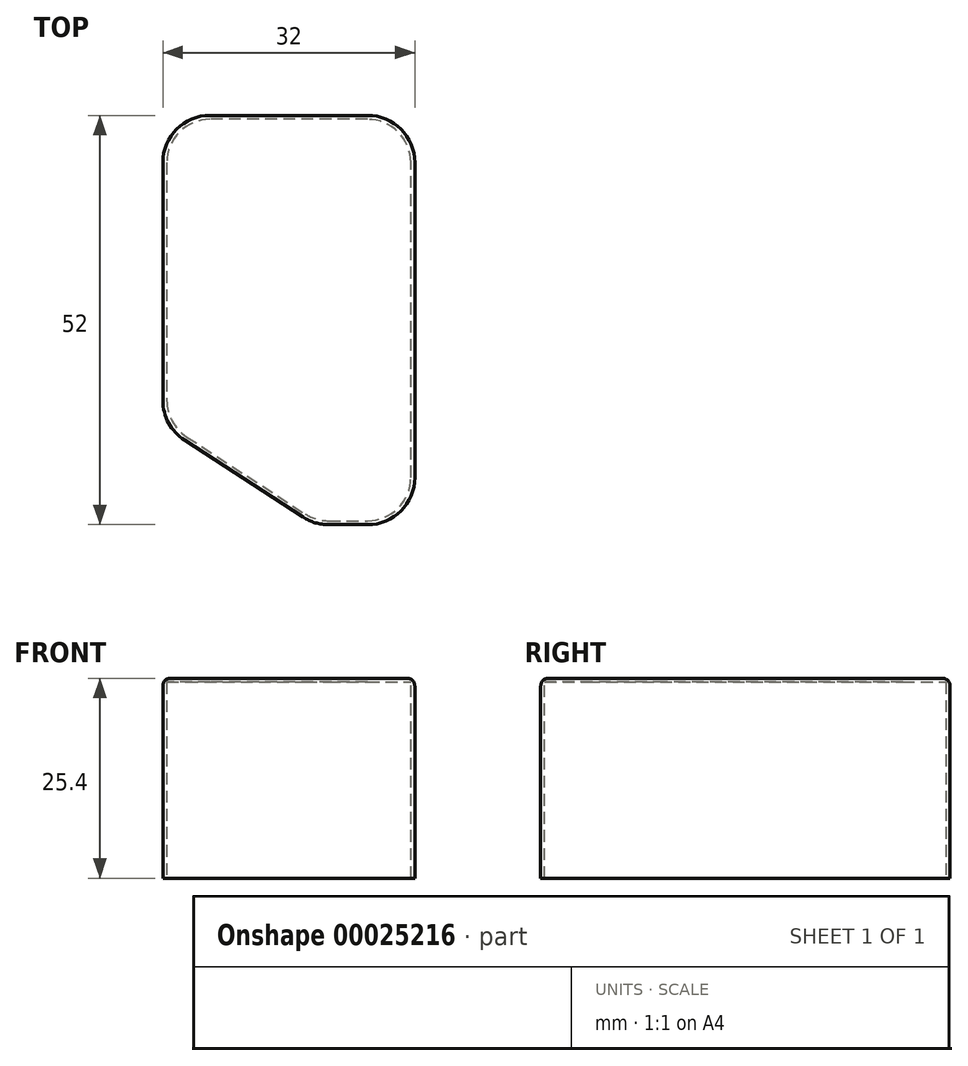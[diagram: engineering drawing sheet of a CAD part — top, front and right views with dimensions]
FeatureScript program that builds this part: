
annotation { "Feature Type Name" : "Feature", "Feature Type Description" : "" }
export const myFeature = defineFeature(function(context is Context, id is Id, definition is map)
    precondition{}
    {
        {
            var Q0;
            Q0=qCreatedBy(makeId("Top.planeOp"),FACE);
            var sketch = newSketch(context, id + "F0", { "sketchPlane" : qUnion([Q0])});
            skArc(sketch, "E0.0", {"start": v(9.6, -23) * mm, "mid": v(13.85, -21.24) * mm, "end": v(15.6, -17) * mm});
            skLineSegment(sketch, "E0.1", {"start": v(4.66, -23) * mm, "end": v(9.6, -23) * mm});
            skArc(sketch, "E0.2", {"start": v(1.4, -22.02) * mm, "mid": v(2.96, -22.75) * mm, "end": v(4.66, -23) * mm});
            skLineSegment(sketch, "E0.3", {"start": v(-13.66, -12.24) * mm, "end": v(1.4, -22.02) * mm});
            skArc(sketch, "E0.4", {"start": v(-16.4, -7.21) * mm, "mid": v(-15.67, -10.07) * mm, "end": v(-13.66, -12.24) * mm});
            skLineSegment(sketch, "E0.5", {"start": v(15.6, -17) * mm, "end": v(15.6, 23) * mm});
            skLineSegment(sketch, "E0.6", {"start": v(-16.4, 23) * mm, "end": v(-16.4, -7.21) * mm});
            skArc(sketch, "E0.7", {"start": v(-10.4, 29) * mm, "mid": v(-14.64, 27.25) * mm, "end": v(-16.4, 23) * mm});
            skLineSegment(sketch, "E0.8", {"start": v(9.6, 29) * mm, "end": v(-10.4, 29) * mm});
            skArc(sketch, "E0.9", {"start": v(15.6, 23) * mm, "mid": v(13.85, 27.25) * mm, "end": v(9.6, 29) * mm});
            skSolve(sketch);
        }
        {
            var Q0;
            Q0=makeQuery(id+"F0.imprint","IMPRINT",FACE,{"disambiguationData":[TD([[makeQuery(id+"F0.imprint","IMPRINT",EDGE,{"derivedFrom":sQuery(id+"F0.wireOp",EDGE,"E0.0")}),1.0]])]});
            extrude(context, id + "F1", {"entities" : qUnion([Q0]), "depth" : 25.4 * mm});
        }
        {
            var Q0;
            Q0=makeQuery(id+"F1.opExtrude","CAP_FACE",FACE,{"disambiguationData":[OSD([sQuery(id+"F0.wireOp",EDGE,"E0.0"),sQuery(id+"F0.wireOp",EDGE,"E0.1"),sQuery(id+"F0.wireOp",EDGE,"E0.2"),sQuery(id+"F0.wireOp",EDGE,"E0.3"),sQuery(id+"F0.wireOp",EDGE,"E0.4"),sQuery(id+"F0.wireOp",EDGE,"E0.5"),sQuery(id+"F0.wireOp",EDGE,"E0.6"),sQuery(id+"F0.wireOp",EDGE,"E0.7"),sQuery(id+"F0.wireOp",EDGE,"E0.8"),sQuery(id+"F0.wireOp",EDGE,"E0.9")])],"isStart":true});
            shell(context, id + "F2", {"entities" : qUnion([Q0]), "thickness" : 0.5 * mm});
        }
        {
            var Q0;
            Q0=makeQuery(id+"F1.opExtrude","CAP_EDGE",EDGE,{"disambiguationData":[OSD([sQuery(id+"F0.wireOp",EDGE,"E0.3")])],"isStart":false});
            fillet(context, id + "F3", {"entities" : qUnion([Q0]), "radius" : 1 * mm, "tangentPropagation" : true, "allowEdgeOverflow" : false});
        }
    });
